# Revit family: Lighting-Surface-Teron-Guardian-LED2
name_source: partatom
category: Lighting Fixtures
revit_build: Autodesk Revit 2014 (Build: 20130308_1515(x64)
units: mm (PartAtom-declared; Revit-internal decimal feet)

## types (1)
- See Type Catalog
    ADA Compliant = Yes
    Apparent Load = 0 VA
    Assembly Code = D5020200
    Color Filter = 16777215
    Default Elevation = 48 "
    Description = Sconce Light
    Dimming Lamp Color Temperature Shift = <None>
    Driver = See Type Catalog
    Emit Shape Visible in Rendering = No
    Emit from Rectangle Length = 16 "
    Emit from Rectangle Width = 9 "
    Finish = See Type Catalog
    Finish Material = <By Category>
    Height = 4 "
    Lamp = LED
    Lamp Quantity = LED
    Length = 16 "
    Lens Opening = 11.06 "
    Manufacturer = Teron Lighting Inc.
    Model = See Type Catalog
    Number of Poles = 1
    Photometric Web File = Guardian-W-F213QE.ies
    Power Factor = 1
    Product Documentation Link = http://35ce88c86d2ba5f3955c-18d6ce0dad087656504498556450364f.r15.cf1.rackcdn.com
    Product Page URL = http://teronlighting.com
    Shade Solid Height = 3.75 "
    Shade Solid Width = 8.5 "
    Shade Void Height = 3.625 "
    Shade Void Width = 8.25 "
    Shade Voide Height = 3.625 "
    Tilt Angle = 0.00°
    URL = http://teronlighting.com
    Voltage = 0 V
    Width = 9 "

## geometry (parser evidence)
native form markers: Sweep x3
no freeform markers — native parametric forms only
